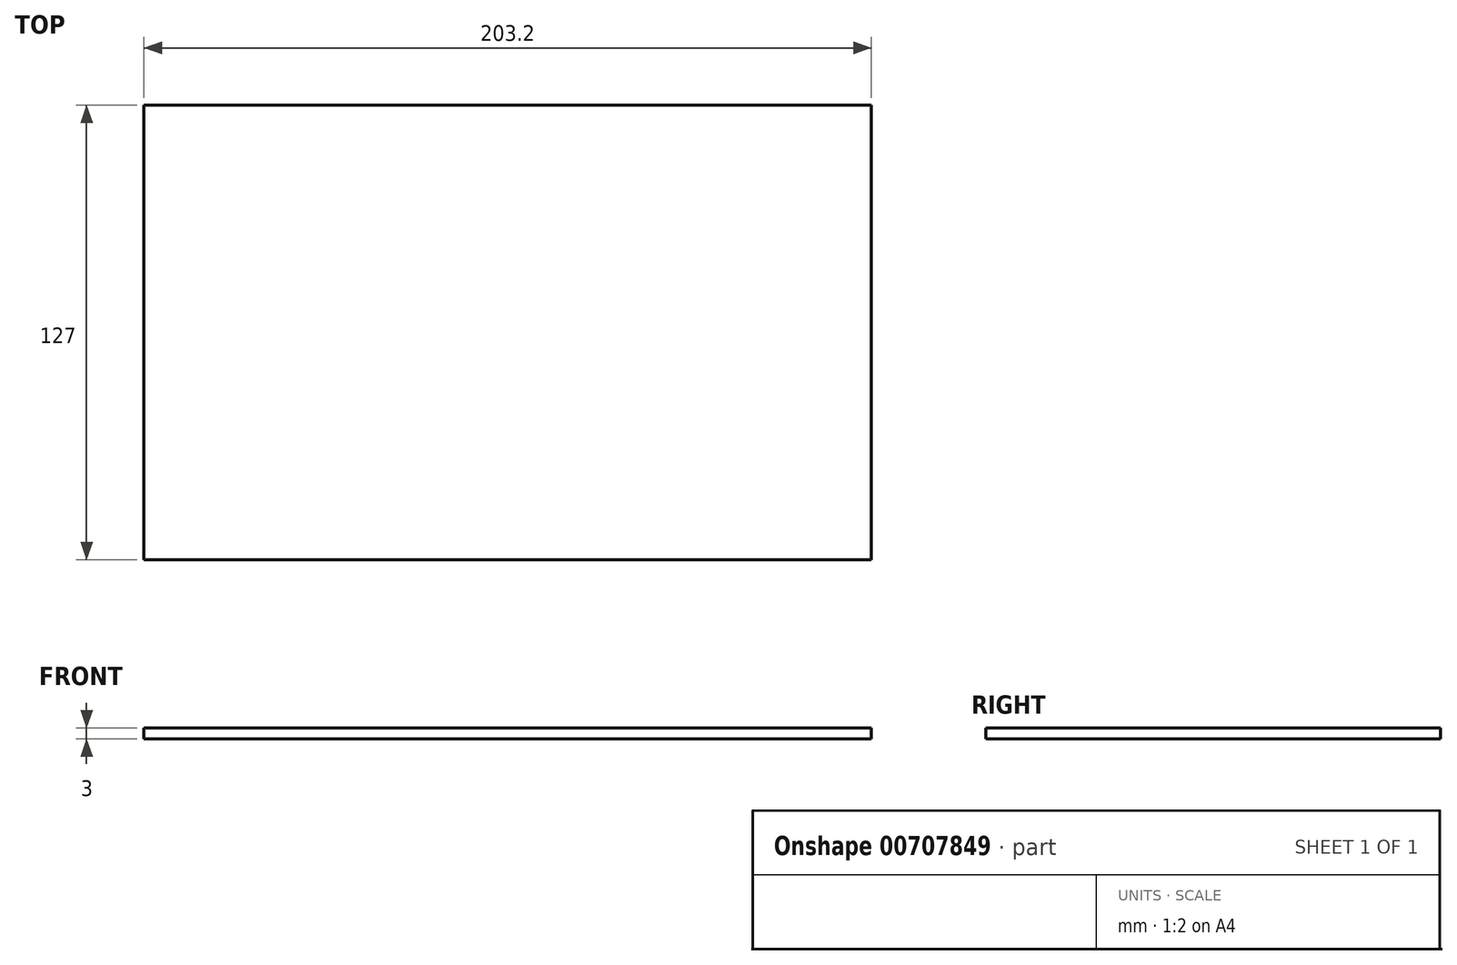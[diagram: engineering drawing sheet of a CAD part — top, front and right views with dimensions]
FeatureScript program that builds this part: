
annotation { "Feature Type Name" : "Feature", "Feature Type Description" : "" }
export const myFeature = defineFeature(function(context is Context, id is Id, definition is map)
    precondition{}
    {
        {
            var Q0;
            Q0=qCreatedBy(makeId("Top.planeOp"),FACE);
            var sketch = newSketch(context, id + "F0", { "sketchPlane" : qUnion([Q0])});
            skLineSegment(sketch, "E0.bottom", {"start": v(-101.26, 63.82) * mm, "end": v(101.94, 63.82) * mm});
            skLineSegment(sketch, "E0.top", {"start": v(-101.26, -63.18) * mm, "end": v(101.94, -63.18) * mm});
            skLineSegment(sketch, "E0.left", {"start": v(-101.26, 63.82) * mm, "end": v(-101.26, -63.18) * mm});
            skLineSegment(sketch, "E0.right", {"start": v(101.94, 63.82) * mm, "end": v(101.94, -63.18) * mm});
            skSolve(sketch);
        }
        {
            var Q0;
            Q0 = qSketchRegion(id + "F0", true);
            extrude(context, id + "F1", {"entities" : qUnion([Q0]), "depth" : 3 * mm, "offsetDistance" : 25.4 * mm});
        }
    });
